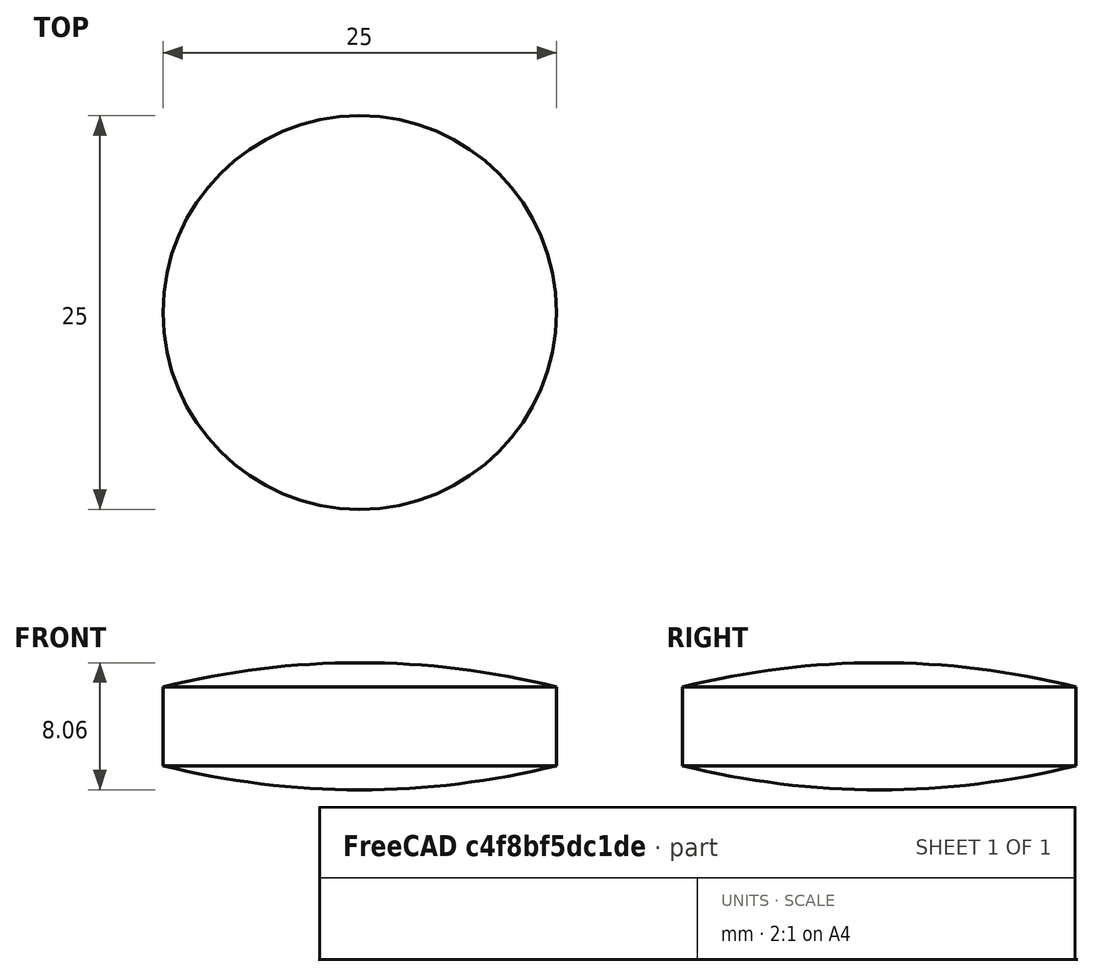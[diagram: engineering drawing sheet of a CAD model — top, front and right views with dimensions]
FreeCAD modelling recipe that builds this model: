
FCSTD DOCUMENT  (FreeCAD 0.21R0.20.1)
Label: BiconvexSpherical
License: All rights reserved
LicenseURL: https://en.wikipedia.org/wiki/All_rights_reserved
objects: Part::Sphere×2, Part::MultiCommon×2, Spreadsheet::Sheet×1, Part::Cylinder×1
note: 5 computed .brp shape members not serialized (recipe doc carries the construction recipe); baked Part::Feature solids carry a one-line shape summary decoded from their .brp

FEATURE [Spreadsheet::Sheet] Spreadsheet  label="LensParameters"
  cells = A2=Diameter; B2(lens_diameter)=25; E2=Back focal length; F2(back_focal_length)==focal_length_effective - center_thickness / 2; H2=List of interesting materials:; I2=Material; J2=Refractive index; K2=Extinction coefficient; L2=Transmission spectrum; A3=Effective Focal Length; B3(focal_length_effective)=50; E3=Radius of curvature; F3(radiusOfCurvature)==2 * (n_material - 1) * focal_length_effective; I3=N-BK7; J3=1.52; K3='9.752500000000001e-09; L3=350nm - 2um; A4=Medium refractive index; B4(n0_medium)=1; E4=f-Number; F4(f_number)==focal_length_effective / lens_diameter; I4=UV Fused Silica; J4=1.46; L4=185nm - 2.1um; A5=Material refractive index; B5(n_material)=1.5168; C5=(BK7 has about 1.5168); E5=Numerical aperture; F5(numerical_aperture)==n0_medium * sin(atan(lens_diameter / (2 * focal_length_effective))); I5=CaF2; J5=1.4339; L5=180nm - 8um; A6=Extinction coefficient; B6(extinction_coefficient)=9.752500000000001e-09; C6=(BK7 has about 9.7525e-9); E6=Center thickness; F6(center_thickness)==edge_thickness - 2 * sqrt(radiusOfCurvature ^ 2 - (lens_diameter / 2) ^ 2) + 2 * radiusOfCurvature; I6=MgF2; J6=2.6123; L6=200nm - 6um; A7=Edge thickness; B7(edge_thickness)=5; E7=Sphere center offset; F7(sphere_center_offset)==(2 * radiusOfCurvature - center_thickness) / 2; I7=SF11; J7=1.00072905; L7=420nm - 2.3um; I8=Ge; J8=5.6959; K8=1.4059; L8=2.0um - 16um; I9=ZnSe; J9=2.6018; L9=600nm - 16um; I10=Si; J10=3.9485; K10=0.027397; L10=1.2um - 8um
FEATURE [Part::Sphere] Sphere
  Angle1 = -90
  Angle2 = 90
  Angle3 = 360
  AttacherType = Attacher::AttachEngine3D
  Placement = pos=(0,0,47.6455) rot=(0,0,1;0rad)
  Radius = 51.68
  expr: .Placement.Base.z = <<LensParameters>>.sphere_center_offset
  expr: Radius = <<LensParameters>>.radiusOfCurvature
FEATURE [Part::Sphere] Sphere001
  Angle1 = -90
  Angle2 = 90
  Angle3 = 360
  AttacherType = Attacher::AttachEngine3D
  Placement = pos=(0,0,-47.6455) rot=(0,0,1;0rad)
  Radius = 51.68
  expr: .Placement.Base.z = -<<LensParameters>>.sphere_center_offset
  expr: Radius = <<LensParameters>>.radiusOfCurvature
FEATURE [Part::MultiCommon] Common
  Shapes = -> [Sphere,Sphere001]
FEATURE [Part::Cylinder] Cylinder
  Angle = 360
  AttacherType = Attacher::AttachEngine3D
  FirstAngle = 0
  Height = 8.06898
  Placement = pos=(0,0,-4.03449) rot=(0,0,1;0rad)
  Radius = 12.5
  SecondAngle = 0
  expr: .Placement.Base.z = -<<LensParameters>>.center_thickness / 2
  expr: Height = <<LensParameters>>.center_thickness
  expr: Radius = <<LensParameters>>.lens_diameter / 2
FEATURE [Part::MultiCommon] Common001  label="Lens"
  Shapes = -> [Cylinder,Common]
